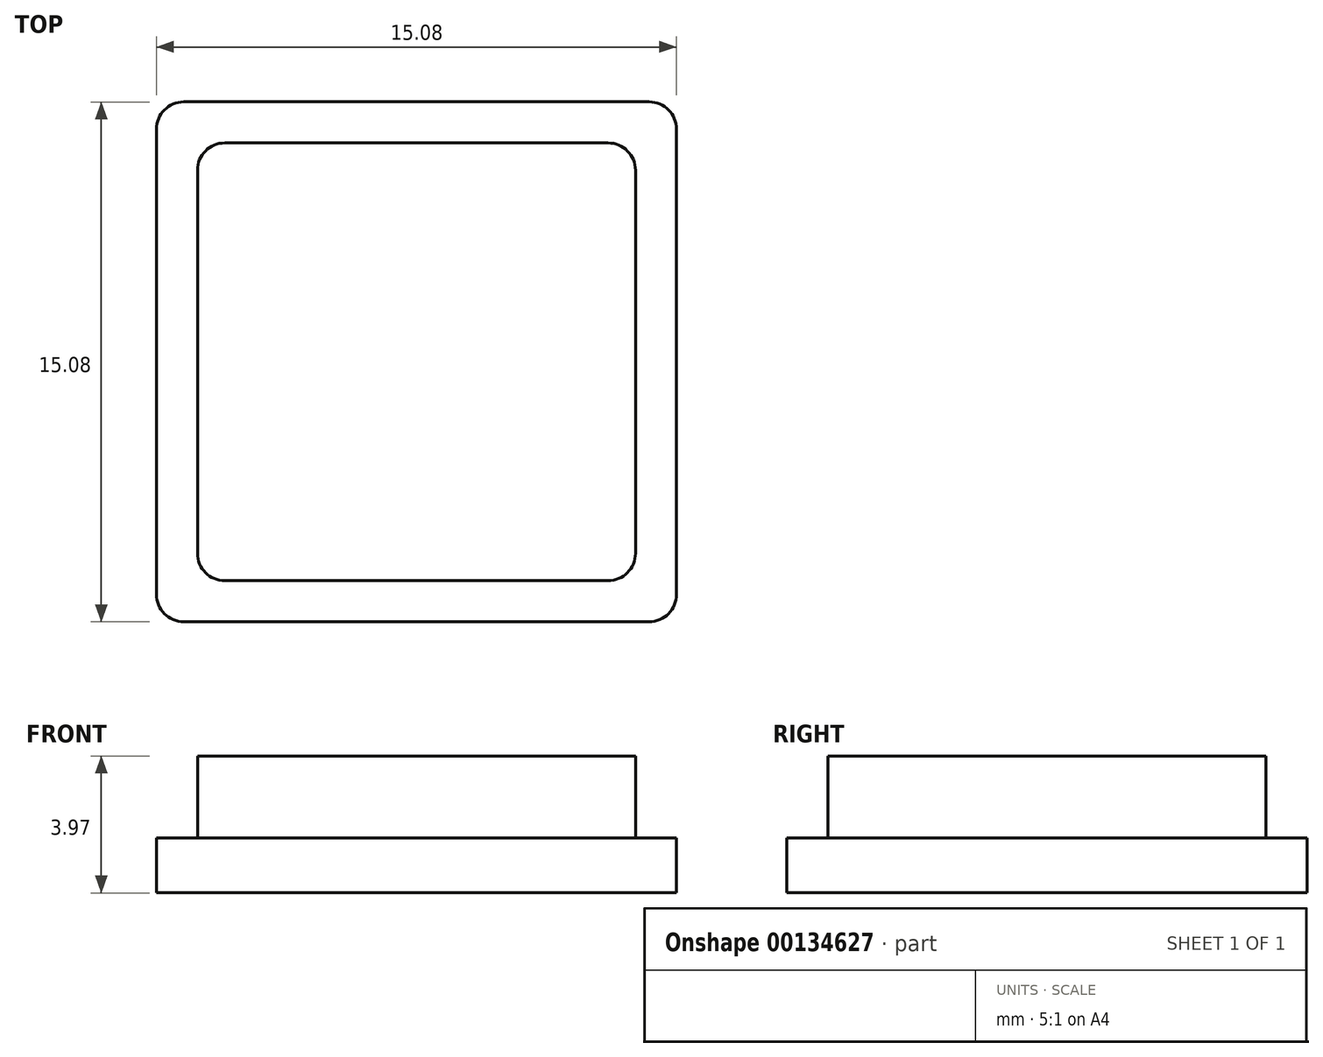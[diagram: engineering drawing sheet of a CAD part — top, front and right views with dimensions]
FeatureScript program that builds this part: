
annotation { "Feature Type Name" : "Feature", "Feature Type Description" : "" }
export const myFeature = defineFeature(function(context is Context, id is Id, definition is map)
    precondition{}
    {
        {
            var Q0;
            Q0=qCreatedBy(makeId("Top.planeOp"),FACE);
            var sketch = newSketch(context, id + "F0", { "sketchPlane" : qUnion([Q0])});
            skLineSegment(sketch, "E0.bottom", {"start": v(5.56, -6.35) * mm, "end": v(-5.56, -6.35) * mm});
            skLineSegment(sketch, "E0.top", {"start": v(5.56, 6.35) * mm, "end": v(-5.56, 6.35) * mm});
            skLineSegment(sketch, "E0.left", {"start": v(6.35, -5.56) * mm, "end": v(6.35, 5.56) * mm});
            skLineSegment(sketch, "E0.right", {"start": v(-6.35, -5.56) * mm, "end": v(-6.35, 5.56) * mm});
            skPoint(sketch, "E0.middle", {"position": v(0, 0) * mm});
            skPoint(sketch, "E1.visualSharp", {"position": v(-6.35, 6.35) * mm});
            skArc(sketch, "E1.filletArc", {"start": v(-5.56, 6.35) * mm, "mid": v(-6.12, 6.12) * mm, "end": v(-6.35, 5.56) * mm});
            skPoint(sketch, "E2.visualSharp", {"position": v(6.35, 6.35) * mm});
            skArc(sketch, "E2.filletArc", {"start": v(6.35, 5.56) * mm, "mid": v(6.12, 6.12) * mm, "end": v(5.56, 6.35) * mm});
            skPoint(sketch, "E3.visualSharp", {"position": v(6.35, -6.35) * mm});
            skArc(sketch, "E3.filletArc", {"start": v(5.56, -6.35) * mm, "mid": v(6.12, -6.12) * mm, "end": v(6.35, -5.56) * mm});
            skPoint(sketch, "E4.visualSharp", {"position": v(-6.35, -6.35) * mm});
            skArc(sketch, "E4.filletArc", {"start": v(-6.35, -5.56) * mm, "mid": v(-6.12, -6.12) * mm, "end": v(-5.56, -6.35) * mm});
            skSolve(sketch);
        }
        {
            var Q0;
            Q0 = qSketchRegion(id + "F0", true);
            extrude(context, id + "F1", {"entities" : qUnion([Q0]), "depth" : 2.38 * mm});
        }
        {
            var Q0;
            Q0=makeQuery(id+"F1.opExtrude","CAP_FACE",FACE,{"disambiguationData":[OSD([sQuery(id+"F0.wireOp",EDGE,"E0.bottom"),sQuery(id+"F0.wireOp",EDGE,"E0.top"),sQuery(id+"F0.wireOp",EDGE,"E0.left"),sQuery(id+"F0.wireOp",EDGE,"E0.right"),sQuery(id+"F0.wireOp",EDGE,"E1.filletArc"),sQuery(id+"F0.wireOp",EDGE,"E2.filletArc"),sQuery(id+"F0.wireOp",EDGE,"E3.filletArc"),sQuery(id+"F0.wireOp",EDGE,"E4.filletArc")])],"isStart":true});
            var sketch = newSketch(context, id + "F2", { "sketchPlane" : qUnion([Q0])});
            skLineSegment(sketch, "E5.0.0", {"start": v(5.56, 6.35) * mm, "end": v(-5.56, 6.35) * mm});
            skArc(sketch, "E5.0.1", {"start": v(-5.56, 6.35) * mm, "mid": v(-6.12, 6.12) * mm, "end": v(-6.35, 5.56) * mm});
            skLineSegment(sketch, "E5.0.2", {"start": v(-6.35, 5.56) * mm, "end": v(-6.35, -5.56) * mm});
            skArc(sketch, "E5.0.3", {"start": v(-6.35, -5.56) * mm, "mid": v(-6.12, -6.12) * mm, "end": v(-5.56, -6.35) * mm});
            skLineSegment(sketch, "E5.0.4", {"start": v(-5.56, -6.35) * mm, "end": v(5.56, -6.35) * mm});
            skArc(sketch, "E5.0.5", {"start": v(5.56, -6.35) * mm, "mid": v(6.12, -6.12) * mm, "end": v(6.35, -5.56) * mm});
            skLineSegment(sketch, "E5.0.6", {"start": v(6.35, -5.56) * mm, "end": v(6.35, 5.56) * mm});
            skArc(sketch, "E5.0.7", {"start": v(6.35, 5.56) * mm, "mid": v(6.12, 6.12) * mm, "end": v(5.56, 6.35) * mm});
            skLineSegment(sketch, "E6.bottom", {"start": v(-6.75, 7.54) * mm, "end": v(6.75, 7.54) * mm});
            skLineSegment(sketch, "E6.top", {"start": v(-6.75, -7.54) * mm, "end": v(6.75, -7.54) * mm});
            skLineSegment(sketch, "E6.left", {"start": v(-7.54, 6.75) * mm, "end": v(-7.54, -6.75) * mm});
            skLineSegment(sketch, "E6.right", {"start": v(7.54, 6.75) * mm, "end": v(7.54, -6.75) * mm});
            skPoint(sketch, "E7.visualSharp", {"position": v(-7.54, 7.54) * mm});
            skArc(sketch, "E7.filletArc", {"start": v(-6.75, 7.54) * mm, "mid": v(-7.3, 7.3) * mm, "end": v(-7.54, 6.75) * mm});
            skPoint(sketch, "E8.visualSharp", {"position": v(7.54, 7.54) * mm});
            skArc(sketch, "E8.filletArc", {"start": v(7.54, 6.75) * mm, "mid": v(7.3, 7.3) * mm, "end": v(6.75, 7.54) * mm});
            skPoint(sketch, "E9.visualSharp", {"position": v(7.54, -7.54) * mm});
            skArc(sketch, "E9.filletArc", {"start": v(6.75, -7.54) * mm, "mid": v(7.3, -7.3) * mm, "end": v(7.54, -6.75) * mm});
            skPoint(sketch, "E10.visualSharp", {"position": v(-7.54, -7.54) * mm});
            skArc(sketch, "E10.filletArc", {"start": v(-7.54, -6.75) * mm, "mid": v(-7.3, -7.3) * mm, "end": v(-6.75, -7.54) * mm});
            skSolve(sketch);
        }
        {
            var Q0;
            Q0 = qSketchRegion(id + "F2", true);
            var Q1;
            Q1=makeQuery(id+"F2.imprint","IMPRINT",FACE,{"disambiguationData":[TD([[makeQuery(id+"F2.imprint","IMPRINT",EDGE,{"derivedFrom":sQuery(id+"F2.wireOp",EDGE,"E5.0.0")}),1.0]])]});
            extrude(context, id + "F3", {"entities" : qUnion([Q0, Q1]), "operationType" : NewBodyOperationType.ADD, "depth" : 1.59 * mm});
        }
    });
